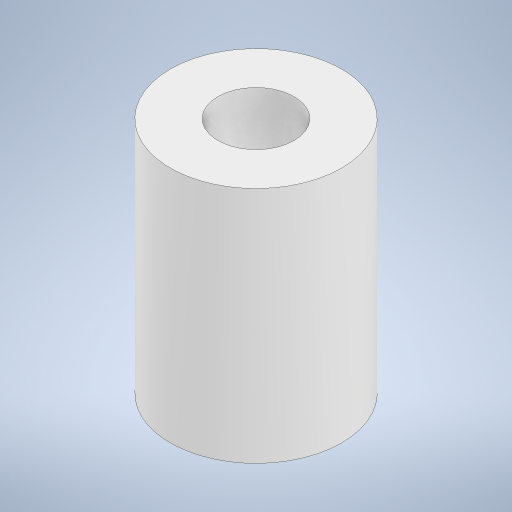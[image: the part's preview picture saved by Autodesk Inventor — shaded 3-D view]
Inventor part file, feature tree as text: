
AUTODESK INVENTOR PART (.ipt)
format: ipt  version: 2024 (Build 280153000, 153)  size: 207,872 bytes
history: native  units: in
note: dims shown in document units (in); Inventor stores cm internally (conversion verified against a paired STEP export)
features: extrude x1, sketch x1
ambient origin geometry x8: Origin, YZ Plane, XZ Plane, XY Plane, X Axis, Y Axis, Z Axis, Center Point
bodies: Solid1 (feature_tree)
feature tree (2):
  extrude  "Extrusion1"  Depth=0.625in
  sketch  "Sketch1"  dims[d0=0.2in d1=0.125in d2=0.625in d3=0.0in]
